# Revit family: Condensing-Storage-Water-Heater-Gas_AO_Smith-BFC_60_G
name_source: partatom
category: Mechanical Equipment
revit_build: Autodesk Revit 2014 (Build: 20130308_1515(x64)
units: mm (PartAtom-declared; Revit-internal decimal feet)

## types (1)
- Condensing-Storage-Water-Heater-Gas_AO_Smith-BFC_60_G
    (Additional Control) Frequency = 0 Hz
    (Additional Control) Phase = 1
    (Additional Control) Power Consumption (nominal) = 0 W
    (Additional Control) Voltage = 0 V
    1e Maintenance (check-up) = 3 months after installation
    2nd Maintenance (general maintenance) = 12 months after installation
    APS Pressure < = 115.0 Pa
    Assembly Code = D3010
    BIM Content Developer = CAD & Company
    CE-PIN = 0063BU3889
    Co2 Emissions (tol. +/- 1.0) vol% = 9.0
    Cold Water Connection R = 1 1/2"
    Condens Discharge Connection = 40 mm  [stored 0.131234 ft]
    Default Setpoint = 65 °C
    Description = Condensing High Efficiency Storage Water Heater
    Destination / Country = UK & Ireland
    Diameter = 705 mm
    Drain Valve Connection Rp = 1"
    Draw-off Capacity @ ΔT = 28°C after 120 min. = 4200.0 L
    Draw-off Capacity @ ΔT = 28°C after 30 min. = 1500.0 L
    Draw-off Capacity @ ΔT = 28°C after 60 min. = 2400.0 L
    Draw-off Capacity @ ΔT = 28°C after 90 min. = 3300.0 L
    Draw-off Capacity @ ΔT = 44°C after 120 min. = 2700.0 L
    Draw-off Capacity @ ΔT = 44°C after 30 min. = 840.0 L
    Draw-off Capacity @ ΔT = 44°C after 60 min. = 1500.0 L
    Draw-off Capacity @ ΔT = 44°C after 90 min. = 2100.0 L
    Draw-off Capacity @ ΔT = 50°C after 120 min. = 2300.0 L
    Draw-off Capacity @ ΔT = 50°C after 30 min. = 720.0 L
    Draw-off Capacity @ ΔT = 50°C after 60 min. = 1300.0 L
    Draw-off Capacity @ ΔT = 50°C after 90 min. = 1800.0 L
    Draw-off Capacity @ ΔT = 55°C after 120 min. = 2100.0 L
    Draw-off Capacity @ ΔT = 55°C after 30 min. = 630.0 L
    Draw-off Capacity @ ΔT = 55°C after 60 min. = 1100.0 L
    Draw-off Capacity @ ΔT = 55°C after 90 min. = 1600.0 L
    Draw-off Capacity @ ΔT = 70°C after 120 min. = 1600.0 L
    Draw-off Capacity @ ΔT = 70°C after 30 min. = 440.0 L
    Draw-off Capacity @ ΔT = 70°C after 60 min. = 810.0 L
    Draw-off Capacity @ ΔT = 70°C after 90 min. = 1200.0 L
    Empty Weight = 214 kg
    Energy Efficiency Rating (Hi, acc NEN-EN 89-1999) = 106
    Energy Efficiency Rating (Hs, acc NEN-EN 89-1999) = 95
    Flue Diameter - concentric system = 100/150 mm/mm
    Flue Diameter - parallel system = 100 mm  [stored 0.328084 ft]
    Flue Diameter - water heater = 100/150 mm/mm
    Frequency = 50 Hz
    Gas Category = II2H3P
    Gas Connection R = 3/4"
    Gas Flow Rate - Mass kg/h = 0
    Gas Flow Rate - Volume ltr/hr = 6
    Heating Up Time @ ΔT = 28°C = 12
    Heating Up Time @ ΔT = 44°C = 19
    Heating Up Time @ ΔT = 50°C = 21
    Heating Up Time @ ΔT = 55°C = 23
    Heating Up Time @ ΔT = 70°C = 30
    Height = 1910 mm  [stored 6.2664 ft]
    Height Air Inlet = 1905 mm
    Height Cold water Intlet = 160 mm  [stored 0.524934 ft]
    Height Flue Outlet = 1905 mm
    Height Gas Connection = 1815 mm
    Height Warm Water Outlet = 1910 mm  [stored 6.2664 ft]
    Hot / Warm Water Connection R = 1 1/2"
    Installation Type = B23/C13/C33/C43/C53/C63
    Insulation Thickness = 50 mm  [stored 0.164042 ft]
    Length = 0 mm  [stored 0 ft]
    Maintenance Interval = 12 months
    Manufacturer = A.O. Smith Water Products Company b.v.
    Manufacturer Number = E 7110
    Max. Flue Gas Outlet Temperature = 65 °C
    Max. Operating Pressure = 800000.0 Pa
    Max. Setpoint = 80 °C
    Min. Setpoint = 40 °C
    Model = BFC 60 G
    NOx Emissions (air free, 0% O2) ppm = 27
    NOx Emissions mg/kWh = 49
    Noice-level dB (A) = 45
    Nominal Heat Input (Gross) = 63300 W
    Nominal Heat Input (Net) = 57000 W
    Nominal Output = 60400 W
    Operating Weight = 582 kg
    Packaging Height = 2080 mm
    Packaging Length = 950 mm
    Packaging Width = 790 mm
    Phase = 1
    Power Consumption (nominal) = 115 W
    Product Documentation Link = http://www.aosmithinternational.com
    Product Instruction Link = http://www.aosmith.co.uk
    Recovery Rate @ ΔT = 28°C = 1900.0 L/s
    Recovery Rate @ ΔT = 44°C = 1200.0 L/s
    Recovery Rate @ ΔT = 50°C = 1100.0 L/s
    Recovery Rate @ ΔT = 55°C = 950.0 L/s
    Recovery Rate @ ΔT = 70°C = 750.0 L/s
    Seasonal Energy Efficiency Rating = 95
    Serial Number = 8717449113872
    Stand-by Loss = 0 W
    Stand-by Loss - daily (24h) = 0 W
    Standard Set For = G20
    Storage Capacity = 368.0 L
    Supply Pressure = 2000.0 Pa
    T&P Connection Rp = 1"
    Transport Weight = 235 kg
    Type of Packaging = Plastic Shrink Wrap, Cardboard and Wood
    URL = www.aosmith.co.uk
    Voltage = 230 V
    Warranty on parts = 12 months
    Warranty on tank = 36 months
    Width = 0 mm  [stored 0 ft]

note: [stored X ft] marks values corroborated as IEEE doubles in the binary element streams (Revit-internal decimal feet)

## geometry (parser evidence)
native form markers: Blend x24, Sweep x33
no freeform markers — native parametric forms only
